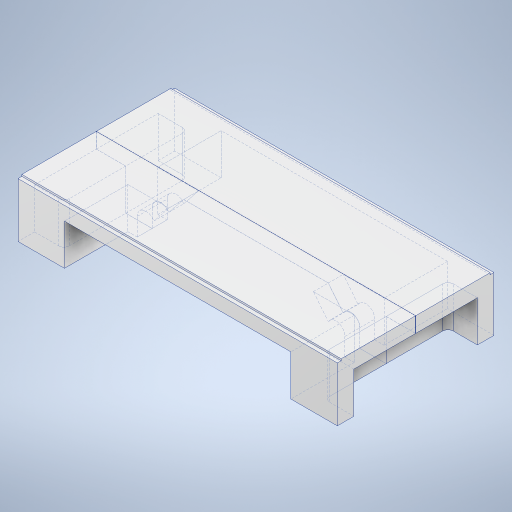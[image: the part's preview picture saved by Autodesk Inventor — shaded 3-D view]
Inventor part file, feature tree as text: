
AUTODESK INVENTOR PART (.ipt)
format: ipt  version: 2024 (Build 280153000, 153)  size: 443,904 bytes
history: native  units: mm
features: sketch x9, extrude x8, projected_geometry x7, fillet x1
ambient origin geometry x8: Origin, YZ Plane, XZ Plane, XY Plane, X Axis, Y Axis, Z Axis, Center Point
bodies: Solid1 (feature_tree)
feature tree (25):
  extrude  "Extrusion1"  Depth=175.0mm
  extrude  "Extrusion2"  Depth=18.0mm TaperAngle=0.0deg
  extrude  "Extrusion3"  Depth=265.893mm
  fillet  "Fillet1"  Radius=265.893mm
  sketch  "Sketch4"  dims[d11=20.0mm d12=20.0mm]
  extrude  "Extrusion4"  Depth=20.0mm
  extrude  "Extrusion5"  Depth=34.5535mm
  extrude  "Extrusion6"  Depth=15.0mm
  extrude  "Extrusion7"  Depth=15.0mm
  extrude  "Extrusion8"  Depth=6.0mm
  sketch  "Sketch1"  dims[d0=175.0mm d1=175.0mm]
  sketch  "Sketch2"  dims[d2=12.0mm d3=0.0mm d6=18.0mm d7=0.0mm]
  sketch  "Sketch3"  dims[d8=100.0mm d9=100.0mm d10=265.893mm]
  projected_geometry  "Projected Loop1"
  sketch  "Sketch5"  dims[d13=34.5535mm d14=34.5535mm]
  sketch  "Sketch6"  dims[d15=48.0mm d16=0.0mm d17=15.0mm]
  sketch  "Sketch7"  dims[d18=15.0mm d19=15.0mm]
  projected_geometry  "Projected Loop2"
  projected_geometry  "Projected Loop3"
  projected_geometry  "Projected Loop4"
  projected_geometry  "Projected Loop5"
  sketch  "Sketch8"  dims[d20=15.0mm d21=6.0mm]
  projected_geometry  "Projected Loop6"
  sketch  "Sketch9"  dims[d22=50.0mm d23=50.0mm d24=70.0mm d25=70.0mm d26=223.0mm d27=21.4465mm d29=26.925mm d30=26.925mm d31=21.4465mm d32=21.0mm d33=21.0mm d34=12.0mm d35=2.0mm d37=2.0mm d38=54.0mm d39=0.0mm d40=5.0mm d41=5.0mm d42=87.45mm d43=87.45mm d44=98.0mm d45=0.0mm d46=6.0mm d47=0.0mm d48=4.5mm d49=0.0mm d50=4.5mm d51=0.0mm]
  projected_geometry  "Projected Loop7"
